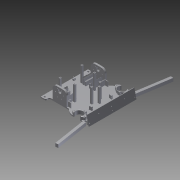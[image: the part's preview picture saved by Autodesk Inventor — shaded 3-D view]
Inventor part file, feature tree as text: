
AUTODESK INVENTOR PART (.ipt)
format: ipt  version: 2011 SP2 (Build 150309200, 309)  size: 1,259,008 bytes
history: native  units: mm
features: extrude x33, sketch x19, projected_geometry x14, fillet x9, mirror x2, plane x1, chamfer x1, hole x1
ambient origin geometry x8: Origin, YZ Plane, XZ Plane, XY Plane, X Axis, Y Axis, Z Axis, Center Point
feature tree (80):
  sketch  "Sketch1"  dims[d0=200.0mm d1=200.0mm]
  extrude  "Extrusion3"  Depth=200.0mm
  extrude  "Extrusion4"  Depth=10.5mm
  extrude  "Extrusion5"  Depth=6.5mm
  extrude  "Extrusion6"  Depth=53.3mm
  extrude  "Extrusion7"  Depth=26.65mm
  sketch  "Sketch4"  dims[d6=6.5mm d8=53.3mm]
  extrude  "Extrusion8"  Depth=5.0mm
  extrude  "Extrusion9"  Depth=5.0mm
  extrude  "Extrusion10"  Depth=4.4mm
  plane  "Work Plane1"
  mirror  "Mirror1"
  sketch  "Sketch9"  dims[d9=53.3mm d10=26.65mm]
  sketch  "Sketch10"  dims[d11=26.65mm d13=5.0mm]
  extrude  "Extrusion16"  Depth=8.0mm
  extrude  "Extrusion17"  Depth=8.0mm
  extrude  "Extrusion18"  Depth=60.0mm
  extrude  "Extrusion19"  Depth=39.0mm
  extrude  "Extrusion20"  Depth=3.65mm
  extrude  "Extrusion21"  Depth=1.5mm
  extrude  "Extrusion22"  Depth=6.6mm
  sketch  "Sketch13"  dims[d18=4.4mm d19=8.0mm]
  extrude  "Extrusion26"  Depth=6.6mm
  extrude  "Extrusion27"  Depth=3.5mm
  extrude  "Extrusion30"  Depth=5.0mm
  extrude  "Extrusion32"  Depth=46.7mm
  extrude  "Extrusion33"  Depth=4.0mm TaperAngle=0.0deg
  extrude  "Extrusion34"  Depth=11.0mm TaperAngle=0.0deg
  chamfer  "Chamfer2"  Distance=55.0mm
  fillet  "Fillet1"  Radius=13.0mm
  extrude  "Extrusion35"  Depth=38.0mm
  extrude  "Extrusion36"  Depth=36.8mm
  sketch  "Sketch21"  dims[d28=1.6mm d29=3.65mm d30=3.65mm]
  extrude  "Extrusion37"  Depth=7.0mm
  extrude  "Extrusion39"  Depth=3.0mm
  extrude  "Extrusion40"  Depth=15.5mm
  fillet  "Fillet2"  Radius=60.0mm
  sketch  "Sketch28"  dims[d44=60.0mm d45=6.6mm]
  extrude  "Extrusion48"  Depth=55.0mm TaperAngle=0.0deg
  extrude  "Extrusion49"  Depth=2.0mm
  extrude  "Extrusion42"  Depth=2.0mm
  extrude  "Extrusion44"  Depth=3.65mm
  fillet  "Fillet4"  Radius=3.65mm
  mirror  "Mirror3"
  fillet  "Fillet3"  Radius=55.0mm
  extrude  "Extrusion45"  Depth=36.8mm
  sketch  "Sketch30"  dims[d49=12.061mm d50=5.0mm]
  extrude  "Extrusion46"  Depth=36.0mm
  extrude  "Extrusion47"  Depth=40.0mm TaperAngle=0.0deg
  hole  "Hole1"  [1 undecoded]
  fillet  "Fillet7"  Radius=23.0mm
  fillet  "Fillet8"  Radius=23.35mm
  fillet  "Fillet9"  Radius=6.15mm
  fillet  "Fillet11"  Radius=2.8mm
  fillet  "Fillet12"  Radius=2.8mm
  sketch  "Sketch2"  dims[d2=10.5mm d3=10.5mm]
  sketch  "Sketch3"  dims[d4=57.861mm d5=6.5mm]
  projected_geometry  "Projected Loop1"
  projected_geometry  "Projected Loop7"
  sketch  "Sketch11"  dims[d14=5.0mm d15=5.0mm]
  sketch  "Sketch12"  dims[d16=6.15mm d17=4.4mm]
  projected_geometry  "Projected Loop8"
  sketch  "Sketch15"  dims[d20=5.0mm d21=8.0mm]
  projected_geometry  "Projected Loop9"
  sketch  "Sketch18"  dims[d22=5.0mm d23=60.0mm]
  projected_geometry  "Projected Loop11"
  sketch  "Sketch20"  dims[d25=138.0mm d27=39.0mm]
  projected_geometry  "Projected Loop12"
  sketch  "Sketch25"  dims[d31=3.0mm d32=0.5mm d34=1.5mm d36=5.0mm]
  sketch  "Sketch27"  dims[d37=3.0mm d38=5.0mm d39=8.15mm d41=6.6mm d42=1.5mm d43=0.5mm]
  projected_geometry  "Projected Loop16"
  sketch  "Sketch29"  dims[d47=11.6mm d48=3.5mm]
  sketch  "Sketch31"  dims[d56=8.15mm d57=46.7mm d58=4.0mm d59=0.0mm d60=11.0mm d61=0.0mm d62=55.0mm d63=0.0mm d64=13.0mm d65=38.0mm d66=36.8mm d67=7.0mm d68=3.0mm d69=15.5mm d70=60.0mm d72=360.0deg d74=55.0mm d75=0.0mm d76=2.0mm d77=2.0mm d78=3.65mm d79=3.65mm d80=55.0mm d81=0.0mm d82=36.8mm d83=36.0mm d84=40.0mm d85=0.0mm d86=40.0mm d87=0.0mm d88=23.0mm d89=0.0mm d90=23.35mm d91=6.15mm d119=2.8mm d120=2.8mm d121=2.8mm d122=2.8mm d135=32.757mm d136=32.757mm d137=80.957mm d138=80.957mm d139=27.264mm d140=20.564mm d141=34.936mm d142=35.936mm d143=2.0mm d144=11.0mm d145=11.0mm d146=2.0mm d147=11.0mm d148=11.0mm d149=2.0mm d150=2.0mm d155=6.0mm d156=6.0mm d157=6.0mm d158=6.0mm d159=3.0mm d160=3.0mm d161=3.0mm d162=3.0mm d163=6.0mm d164=6.0mm d165=3.0mm d166=3.0mm d167=6.0mm d168=6.0mm d169=3.0mm d170=3.0mm d181=3.0mm d182=2.5mm d184=0.0mm d185=0.0mm d186=200.0mm d187=0.0mm d188=200.0mm d189=0.0mm d190=58.0mm d191=0.0mm d192=18.0mm d193=0.0mm d194=40.0mm d195=0.0mm d196=1.570796mm d197=1.570796mm d198=220.0mm d199=220.0mm d200=10.0mm d201=10.0mm d202=5.0mm d203=7.0mm d204=0.0mm d205=0.0mm d215=32.1mm d231=5.0mm d233=12.0mm d234=0.0mm d239=20.0mm d240=0.0mm d256=6.0mm d257=167.0mm d258=6.2mm d259=6.0mm d260=0.0mm d262=22.75mm d266=10.0mm d267=38.9mm d268=5.5mm d269=32.1mm d272=10.0mm d273=12.2mm d276=12.0mm d277=0.0mm d278=28.5mm d279=10.3mm d280=0.0mm d281=5.0mm d282=0.0mm d283=0.5mm d284=5.3mm d285=45.0deg d286=1.0mm d287=5.0mm d288=0.0mm d289=3.0mm d290=3.0mm d291=10.0mm d292=0.0mm d293=6.15mm d294=4.4mm d295=2.0mm d296=3.0mm d297=10.0mm d298=0.0mm d306=41.0mm d307=0.0mm d308=6.0mm d309=6.0mm d310=2.575mm d311=2.575mm d312=2.0mm d313=2.0mm d315=8.956377mm d316=161.0mm d317=10.0mm d318=7.0mm d319=0.0mm d320=32.5mm d335=32.5mm d336=7.0mm d337=12.0mm d338=9.25mm d339=-0.872665mm d343=1.0mm d344=9.25mm d345=-0.872665mm d346=8.0mm d347=4.0mm d348=10.0mm d349=20.0mm d350=0.0mm d351=179.0mm d352=0.0mm d353=179.0mm d354=0.0mm d355=1.5mm d356=3.5mm d357=3.5mm d358=89.5mm d359=89.5mm d360=5.0mm d361=17.5mm d362=2.0mm d363=6.0mm d364=3.0mm d365=2.0mm d366=90.0deg d367=2.0mm d368=3.665191mm d369=6.0mm d370=6.0mm d371=6.0mm d372=6.0mm d373=6.0mm d376=6.0mm d377=2.0mm d378=2.0mm d379=2.0mm d380=3.0mm d382=3.0mm d383=3.0mm d384=3.0mm d386=55.0mm d387=0.0mm d388=40.0mm d389=0.0mm d390=26.0mm d391=69.0mm d392=48.0mm d393=3.0mm d394=13.0mm d395=13.0mm d396=3.0mm d399=0.5mm d400=1.0mm d401=0.5mm d403=15.0mm d404=1.0mm]
  projected_geometry  "Projected Loop17"
  projected_geometry  "Projected Loop18"
  projected_geometry  "Projected Loop19"
  projected_geometry  "Projected Loop20"
  projected_geometry  "Projected Loop21"
  projected_geometry  "Projected Loop22"
  projected_geometry  "Projected Loop23"
note: 1 required parameter value undecoded (feature->parameter linkage not recoverable at this tier; creation-order binding heuristic only, values carry confidence <= 0.55)
